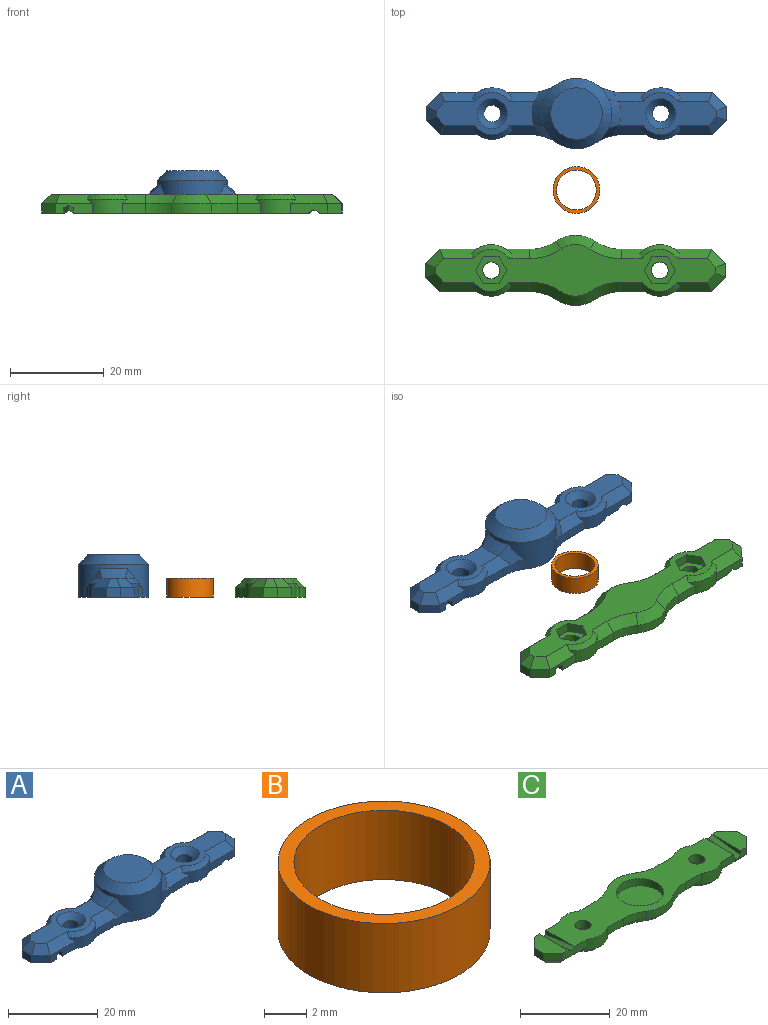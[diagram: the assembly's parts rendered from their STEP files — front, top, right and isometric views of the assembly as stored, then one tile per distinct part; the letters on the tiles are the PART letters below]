
ASSEMBLY  parts=3 mates=2
PART A: 68 faces, bbox 64.1x15.1x9.6 mm
  f0: cylinder r=5.3mm len=10.6mm, axis (0,0,-1), area 233.1mm2, adj f1,f2
  f1: plane 10.6x10.6mm, normal (0,0,-1), area 88.2mm2, adj f0
  f2: plane 50.3x15mm, normal (0,0,-1), area 417.1mm2, adj f0,f5,f8,f39,f44,f45,f46,f47
  f3: plane 11x11mm, normal (0,0,1), area 95mm2, adj f14
  f4: cone r=1.8mm half-angle=45deg, axis (0,0,1), area 31.1mm2, adj f5,f6
  f5: cylinder r=1.8mm len=3.6mm, axis (0,0,-1), area 29.4mm2, adj f2,f4
  f6: plane 20.84x9mm, normal (0,0,1), area 88.6mm2, adj f4,f10,f11,f13,f20,f21,f22,f25
  f7: cone r=1.8mm half-angle=45deg, axis (0,0,1), area 31.1mm2, adj f8,f9
  f8: cylinder r=1.8mm len=3.6mm, axis (0,0,-1), area 29.4mm2, adj f2,f7
  f9: plane 20.84x9mm, normal (0,0,1), area 88.6mm2, adj f7,f12,f15,f16,f17,f18,f19,f23
  f10: plane 7.91x2.07mm, normal (0,-0.71,0.71), area 19mm2, adj f6,f11,f25,f64,f65
  f11: cone r=4.5mm half-angle=45deg, axis (0,0,-1), area 13.1mm2, adj f6,f10,f29,f64
  f12: cone r=9.5mm half-angle=45deg, axis (0,0,-1), area 15.6mm2, adj f9,f31,f32,f33,f34,f62
  f13: cone r=9.5mm half-angle=45deg, axis (0,0,-1), area 15.6mm2, adj f6,f27,f28,f29,f30,f62
  f14: cone r=5.5mm half-angle=45deg, axis (0,0,-1), area 115.5mm2, adj f3,f62
  f15: cone r=4.5mm half-angle=45deg, axis (0,0,-1), area 13.1mm2, adj f9,f16,f34,f60
  f16: plane 7.91x2.07mm, normal (0,-0.71,0.71), area 19mm2, adj f9,f15,f23,f59,f60
  f17: plane 3x2mm, normal (0.71,0,0.71), area 6.1mm2, adj f9,f23,f24,f58
  f18: plane 7.91x2.07mm, normal (0,0.71,0.71), area 19mm2, adj f9,f19,f24,f56,f57
  f19: cone r=4.5mm half-angle=45deg, axis (0,0,-1), area 13.1mm2, adj f9,f18,f31,f56
  f20: cone r=4.5mm half-angle=45deg, axis (0,0,-1), area 13.1mm2, adj f6,f21,f28,f46
  f21: plane 7.91x2.07mm, normal (0,0.71,0.71), area 19mm2, adj f6,f20,f26,f45,f46
  f22: plane 3x2mm, normal (-0.71,0,0.71), area 6.1mm2, adj f6,f25,f26,f42
  f23: plane 3.83x3.83mm, normal (0.5,-0.5,0.71), area 9.7mm2, adj f9,f16,f17,f50
  f24: plane 3.83x3.83mm, normal (0.5,0.5,0.71), area 9.7mm2, adj f9,f17,f18,f53
  f25: plane 3.83x3.83mm, normal (-0.5,-0.5,0.71), area 9.7mm2, adj f6,f10,f22,f40
  f26: plane 3.83x3.83mm, normal (-0.5,0.5,0.71), area 9.7mm2, adj f6,f21,f22,f41
  f27: bspline ~6.6x5.62mm, area 11.4mm2, adj f13,f28,f47,f62
  f28: plane 7.33x2.43mm, normal (0,0.71,0.71), area 16.1mm2, adj f6,f13,f20,f27,f46,f47,f48
  f29: plane 7.33x2.43mm, normal (0,-0.71,0.71), area 16.1mm2, adj f6,f11,f13,f30,f39,f63,f64
  f30: bspline ~6.6x5.62mm, area 11.4mm2, adj f13,f29,f39,f62
  f31: plane 7.33x2.43mm, normal (0,0.71,0.71), area 16.1mm2, adj f9,f12,f19,f32,f54,f55,f56
  f32: bspline ~6.6x5.62mm, area 11.4mm2, adj f12,f31,f54,f62
  f33: bspline ~6.6x5.62mm, area 11.4mm2, adj f12,f34,f49,f62
  f34: plane 7.33x2.43mm, normal (0,-0.71,0.71), area 16.1mm2, adj f9,f12,f15,f33,f49,f60,f61
  f35: plane 9x1.69mm, normal (0.5,-0.11,-0.86), area 10.5mm2, adj f36,f43,f45,f65
  f36: plane 9x1.69mm, normal (-0.5,-0.11,-0.86), area 10.5mm2, adj f35,f44,f45,f65
  f37: plane 9x1.75mm, normal (-0.5,0.11,-0.86), area 11.5mm2, adj f38,f52,f57,f59
  f38: plane 9x1.75mm, normal (0.5,0.11,-0.86), area 11.5mm2, adj f37,f51,f57,f59
  f39: cylinder r=10mm len=5.6mm, axis (0,0,-1), area 10.7mm2, adj f2,f29,f30,f62,f63
  f40: plane 3x3mm, normal (-0.71,-0.71,0), area 8.5mm2, adj f25,f42,f65,f67
  f41: plane 3x3mm, normal (-0.71,0.71,0), area 8.5mm2, adj f26,f42,f45,f67
  f42: plane 3x2mm, normal (-1,0,0), area 6mm2, adj f22,f40,f41,f67
  f43: plane 9x1.13mm, normal (1,0,0), area 5.2mm2, adj f35,f45,f65,f67
  f44: plane 9x1.13mm, normal (-1,0,0), area 5.2mm2, adj f2,f36,f45,f65
  f45: plane 7.84x2mm, normal (0,1,0), area 15mm2, adj f2,f21,f35,f36,f41,f43,f44,f46
  f46: cylinder r=5.5mm len=8.49mm, axis (0,0,-1), area 21.7mm2, adj f2,f20,f21,f28,f45,f48
  f47: cylinder r=10mm len=5.6mm, axis (0,0,-1), area 10.8mm2, adj f2,f27,f28,f48,f62
  f48: plane 5.04x2mm, normal (0,1,0), area 10.1mm2, adj f2,f28,f46,f47
  f49: cylinder r=10mm len=5.6mm, axis (0,0,-1), area 10.8mm2, adj f2,f33,f34,f61,f62
  f50: plane 3x3mm, normal (0.71,-0.71,0), area 8.5mm2, adj f23,f58,f59,f66
  f51: plane 9x1.19mm, normal (1,0,0), area 5.8mm2, adj f2,f38,f57,f59
  f52: plane 9x1.19mm, normal (-1,0,0), area 5.8mm2, adj f37,f57,f59,f66
  f53: plane 3x3mm, normal (0.71,0.71,0), area 8.5mm2, adj f24,f57,f58,f66
  f54: cylinder r=10mm len=5.6mm, axis (0,0,-1), area 10.7mm2, adj f2,f31,f32,f55,f62
  f55: plane 5.04x2mm, normal (0,1,0), area 10.1mm2, adj f2,f31,f54,f56
  f56: cylinder r=5.5mm len=8.49mm, axis (0,0,-1), area 21.7mm2, adj f2,f18,f19,f31,f55,f57
  f57: plane 7.84x2mm, normal (0,1,0), area 12.3mm2, adj f2,f18,f37,f38,f51,f52,f53,f56
  f58: plane 3x2mm, normal (1,0,0), area 6mm2, adj f17,f50,f53,f66
  f59: plane 7.84x2mm, normal (0,-1,0), area 14.8mm2, adj f2,f16,f37,f38,f50,f51,f52,f60
  f60: cylinder r=5.5mm len=8.49mm, axis (0,0,-1), area 21.7mm2, adj f2,f15,f16,f34,f59,f61
  f61: plane 5.04x2mm, normal (0,-1,0), area 10.1mm2, adj f2,f34,f49,f60
  f62: cylinder r=7.5mm len=15mm, axis (0,0,-1), area 191.4mm2, adj f2,f12,f13,f14,f27,f30,f32,f33
  f63: plane 5.04x2mm, normal (0,-1,0), area 10.1mm2, adj f2,f29,f39,f64
  f64: cylinder r=5.5mm len=8.49mm, axis (0,0,-1), area 21.7mm2, adj f2,f10,f11,f29,f63,f65
  f65: plane 7.84x2mm, normal (0,-1,0), area 12.8mm2, adj f2,f10,f35,f36,f40,f43,f44,f64
  f66: plane 9x4.75mm, normal (0,0,-1), area 33.8mm2, adj f50,f52,f53,f57,f58,f59
  f67: plane 9x4.75mm, normal (0,0,-1), area 33.8mm2, adj f40,f41,f42,f43,f45,f65
PART B: 4 faces, bbox 10x10x4 mm
  f0: cylinder r=4.25mm len=8.5mm, axis (0,0,-1), area 106.8mm2, adj f2,f3
  f1: cylinder r=5mm len=10mm, axis (0,0,-1), area 125.7mm2, adj f2,f3
  f2: plane 10x10mm, normal (0,0,1), area 21.8mm2, adj f0,f1
  f3: plane 10x10mm, normal (0,0,-1), area 21.8mm2, adj f0,f1
PART C: 78 faces, bbox 64x15x4 mm
  f0: cylinder r=1.8mm len=3.6mm, axis (0,0,-1), area 22.6mm2, adj f68,f73
  f1: cylinder r=1.8mm len=3.6mm, axis (0,0,-1), area 22.6mm2, adj f61,f73
  f2: plane 7.84x2mm, normal (0,-1,0), area 15mm2, adj f3,f20,f26,f27,f36,f69,f70,f73
  f3: cylinder r=5.5mm len=8.49mm, axis (0,0,-1), area 21.8mm2, adj f2,f4,f36,f45,f54,f73
  f4: plane 5.04x2mm, normal (0,-1,0), area 10.1mm2, adj f3,f23,f45,f73
  f5: cylinder r=7.5mm len=8.4mm, axis (0,0,-1), area 17.8mm2, adj f22,f24,f34,f73
  f6: cylinder r=7.5mm len=8.4mm, axis (0,0,-1), area 17.8mm2, adj f23,f25,f43,f73
  f7: plane 5.04x2mm, normal (0,-1,0), area 10.1mm2, adj f8,f25,f41,f73
  f8: cylinder r=5.5mm len=8.49mm, axis (0,0,-1), area 21.8mm2, adj f7,f9,f41,f46,f52,f73
  f9: plane 7.84x2mm, normal (0,-1,0), area 12.3mm2, adj f8,f18,f28,f29,f46,f71,f72,f73
  f10: plane 3x2mm, normal (1,0,0), area 6mm2, adj f18,f19,f48,f74
  f11: plane 7.84x2mm, normal (0,1,0), area 14.8mm2, adj f12,f19,f28,f29,f50,f71,f72,f73
  f12: cylinder r=5.5mm len=8.49mm, axis (0,0,-1), area 21.8mm2, adj f11,f13,f33,f50,f51,f73
  f13: plane 5.04x2mm, normal (0,1,0), area 10.1mm2, adj f12,f24,f33,f73
  f14: plane 5.04x2mm, normal (0,1,0), area 10.1mm2, adj f15,f22,f31,f73
  f15: cylinder r=5.5mm len=8.49mm, axis (0,0,-1), area 21.8mm2, adj f14,f16,f31,f40,f53,f73
  f16: plane 7.84x2mm, normal (0,1,0), area 12.8mm2, adj f15,f21,f26,f27,f40,f69,f70,f73
  f17: plane 3x2mm, normal (-1,0,0), area 6mm2, adj f20,f21,f38,f75
  f18: plane 3x3mm, normal (0.71,-0.71,0), area 8.5mm2, adj f9,f10,f47,f74
  f19: plane 3x3mm, normal (0.71,0.71,0), area 8.5mm2, adj f10,f11,f49,f74
  f20: plane 3x3mm, normal (-0.71,-0.71,0), area 8.5mm2, adj f2,f17,f37,f75
  f21: plane 3x3mm, normal (-0.71,0.71,0), area 8.5mm2, adj f16,f17,f39,f75
  f22: cylinder r=10mm len=5.6mm, axis (0,0,-1), area 11.9mm2, adj f5,f14,f32,f73
  f23: cylinder r=10mm len=5.6mm, axis (0,0,-1), area 11.9mm2, adj f4,f6,f44,f73
  f24: cylinder r=10mm len=5.6mm, axis (0,0,-1), area 11.9mm2, adj f5,f13,f35,f73
  f25: cylinder r=10mm len=5.6mm, axis (0,0,-1), area 11.9mm2, adj f6,f7,f42,f73
  f26: plane 9x1.13mm, normal (1,0,0), area 5.2mm2, adj f2,f16,f69,f75
  f27: plane 9x1.13mm, normal (-1,0,0), area 5.2mm2, adj f2,f16,f70,f73
  f28: plane 9x1.19mm, normal (-1,0,0), area 5.8mm2, adj f9,f11,f71,f74
  f29: plane 9x1.19mm, normal (1,0,0), area 5.8mm2, adj f9,f11,f72,f73
  f30: plane 60x11mm, normal (0,0,-1), area 328.1mm2, adj f31,f32,f33,f34,f35,f36,f37,f38
  f31: plane 5.04x2mm, normal (0,0.71,-0.71), area 12.2mm2, adj f14,f15,f30,f32,f53
  f32: cone r=10mm half-angle=45deg, axis (0,0,-1), area 18.5mm2, adj f22,f30,f31,f34
  f33: plane 5.04x2mm, normal (0,0.71,-0.71), area 12.2mm2, adj f12,f13,f30,f35,f51
  f34: cone r=7.5mm half-angle=45deg, axis (0,0,1), area 21.9mm2, adj f5,f30,f32,f35
  f35: cone r=10mm half-angle=45deg, axis (0,0,-1), area 18.5mm2, adj f24,f30,f33,f34
  f36: plane 7.84x2mm, normal (0,-0.71,-0.71), area 19mm2, adj f2,f3,f30,f37,f54
  f37: plane 3.83x3.83mm, normal (-0.5,-0.5,-0.71), area 9.7mm2, adj f20,f30,f36,f38
  f38: plane 3x2mm, normal (-0.71,0,-0.71), area 6.1mm2, adj f17,f30,f37,f39
  f39: plane 3.83x3.83mm, normal (-0.5,0.5,-0.71), area 9.7mm2, adj f21,f30,f38,f40
  f40: plane 7.84x2mm, normal (0,0.71,-0.71), area 19mm2, adj f15,f16,f30,f39,f53
  f41: plane 5.04x2mm, normal (0,-0.71,-0.71), area 12.2mm2, adj f7,f8,f30,f42,f52
  f42: cone r=12mm half-angle=45deg, axis (0,0,-1), area 18.5mm2, adj f25,f30,f41,f43
  f43: cone r=5.5mm half-angle=45deg, axis (0,0,1), area 21.9mm2, adj f6,f30,f42,f44
  f44: cone r=12mm half-angle=45deg, axis (0,0,-1), area 18.5mm2, adj f23,f30,f43,f45
  f45: plane 5.04x2mm, normal (0,-0.71,-0.71), area 12.2mm2, adj f3,f4,f30,f44,f54
  f46: plane 7.84x2mm, normal (0,-0.71,-0.71), area 19mm2, adj f8,f9,f30,f47,f52
  f47: plane 3.83x3.83mm, normal (0.5,-0.5,-0.71), area 9.7mm2, adj f18,f30,f46,f48
  f48: plane 3x2mm, normal (0.71,0,-0.71), area 6.1mm2, adj f10,f30,f47,f49
  f49: plane 3.83x3.83mm, normal (0.5,0.5,-0.71), area 9.7mm2, adj f19,f30,f48,f50
  f50: plane 7.84x2mm, normal (0,0.71,-0.71), area 19mm2, adj f11,f12,f30,f49,f51
  f51: cone r=5.5mm half-angle=45deg, axis (0,0,1), area 13.1mm2, adj f12,f30,f33,f50
  f52: cone r=5.5mm half-angle=45deg, axis (0,0,1), area 13.1mm2, adj f8,f30,f41,f46
  f53: cone r=5.5mm half-angle=45deg, axis (0,0,1), area 13.1mm2, adj f15,f30,f31,f40
  f54: cone r=5.5mm half-angle=45deg, axis (0,0,1), area 13.1mm2, adj f3,f30,f36,f45
  f55: plane 2.9x2mm, normal (-0.87,0.5,0), area 6.7mm2, adj f30,f56,f60,f61
  f56: plane 3.35x2mm, normal (0,1,0), area 6.7mm2, adj f30,f55,f57,f61
  f57: plane 2.9x2mm, normal (0.87,0.5,0), area 6.7mm2, adj f30,f56,f58,f61
  f58: plane 2.9x2mm, normal (0.87,-0.5,0), area 6.7mm2, adj f30,f57,f59,f61
  f59: plane 3.35x2mm, normal (0,-1,0), area 6.7mm2, adj f30,f58,f60,f61
  f60: plane 2.9x2mm, normal (-0.87,-0.5,0), area 6.7mm2, adj f30,f55,f59,f61
  f61: plane 6.7x5.8mm, normal (0,0,-1), area 19mm2, adj f1,f55,f56,f57,f58,f59,f60
  f62: plane 2.9x2mm, normal (-0.87,0.5,0), area 6.7mm2, adj f30,f63,f67,f68
  f63: plane 3.35x2mm, normal (0,1,0), area 6.7mm2, adj f30,f62,f64,f68
  f64: plane 2.9x2mm, normal (0.87,0.5,0), area 6.7mm2, adj f30,f63,f65,f68
  f65: plane 2.9x2mm, normal (0.87,-0.5,0), area 6.7mm2, adj f30,f64,f66,f68
  f66: plane 3.35x2mm, normal (0,-1,0), area 6.7mm2, adj f30,f65,f67,f68
  f67: plane 2.9x2mm, normal (-0.87,-0.5,0), area 6.7mm2, adj f30,f62,f66,f68
  f68: plane 6.7x5.8mm, normal (0,0,-1), area 19mm2, adj f0,f62,f63,f64,f65,f66,f67
  f69: plane 9x1.69mm, normal (0.5,0.11,0.86), area 10.5mm2, adj f2,f16,f26,f70
  f70: plane 9x1.69mm, normal (-0.5,0.11,0.86), area 10.5mm2, adj f2,f16,f27,f69
  f71: plane 9x1.75mm, normal (-0.5,-0.11,0.86), area 11.5mm2, adj f9,f11,f28,f72
  f72: plane 9x1.75mm, normal (0.5,-0.11,0.86), area 11.5mm2, adj f9,f11,f29,f71
  f73: plane 50.3x15mm, normal (0,0,1), area 417.1mm2, adj f0,f1,f2,f3,f4,f5,f6,f7
  f74: plane 9x4.75mm, normal (0,0,1), area 33.8mm2, adj f9,f10,f11,f18,f19,f28
  f75: plane 9x4.75mm, normal (0,0,1), area 33.8mm2, adj f2,f16,f17,f20,f21,f26
  f76: plane 10.6x10.6mm, normal (0,0,1), area 88.2mm2, adj f77
  f77: cylinder r=5.3mm len=10.6mm, axis (0,0,-1), area 66.6mm2, adj f73,f76
PLACE A t=(-0.07,16.4,-17.16)mm
PLACE B t=(-0.1,0.07,7.84)mm
PLACE C rot(axis=(1,0,0),180deg) t=(-0.28,-17.09,7.84)mm
MATE planar C.f3 <-> B.f1  axis (0,0,-1) through (-18.28,-17.09,7.84)mm
MATE planar C.f3 <-> A.f20  axis (0,0,-1) through (-18.28,-17.09,7.84)mm
